# Revit family: Domotics-DomesticRanges-GEWISS-SYSTEM_PROTECTION-SPD
name_source: partatom
category: Apparecchi elettrici
revit_build: Autodesk Revit 2016 (Build: 20161004_0715(x64)
units: mm (PartAtom-declared; Revit-internal decimal feet)

## family parameters
Condiviso = Sì
Host = Superficie
Mantenere orientamento annotazione = Sì
Punto di calcolo locali = Sì
Quota connettore circolare = Usa diametro
Taglio con vuoti quando caricato = Sì
Tipo di parte = Normale

## types (2) — shared parameters
Carico apparente = 0 VA
Catalogue = DOMOTICS
Catalogue Range = SYSTEM - DOMESTIC RANGE
Description. = Limiter
Electrocod = 0142
IDF = 9fee14f7-3763-413e-a65c-01745c38fe14
IDT = 0878f3d2-3d3a-42f9-8e58-08a676c8a82a
Immagine tipo = GW21423.jpg
Max.dischargeable energy = 75J
Maximum discharge current = 8 kA (8/20 µs)
N. poli = 1
No. SYSTEM modules = 1
Produttore = GEWISS S.p.A.
Prospetto di default = 1219 mm
SEO = SPD
TIPO = System Limitatore Tensione_GENERICO : GW21423 Limitatore sovratensione 250V 75J nero
Technical sheet = https://www.gewiss.com
URL = https://www.gewiss.com
Version file RFA = 19.4
Volt = 230 V
Voltage = 250 V ac
Voltage: = 250 V ac

## per-type parameters (varying)
| type | Colour | Descrizione | EAN code | Modello |
| GW21423 - Voltage surge limiter 250V 75 j black | Black | VOLTAGE SURGE LIMITER 250V 75 J SY/BK | 8011564129313 | GW21423 |
| GW20423 - Voltage surge limiter 250V 75 j white | White | VOLTAGE SURGE LIMITER 250V 75 J SY/WT | 8011564026049 | GW20423 |

## geometry (parser evidence)
native form markers: Sweep x2
no freeform markers — native parametric forms only
